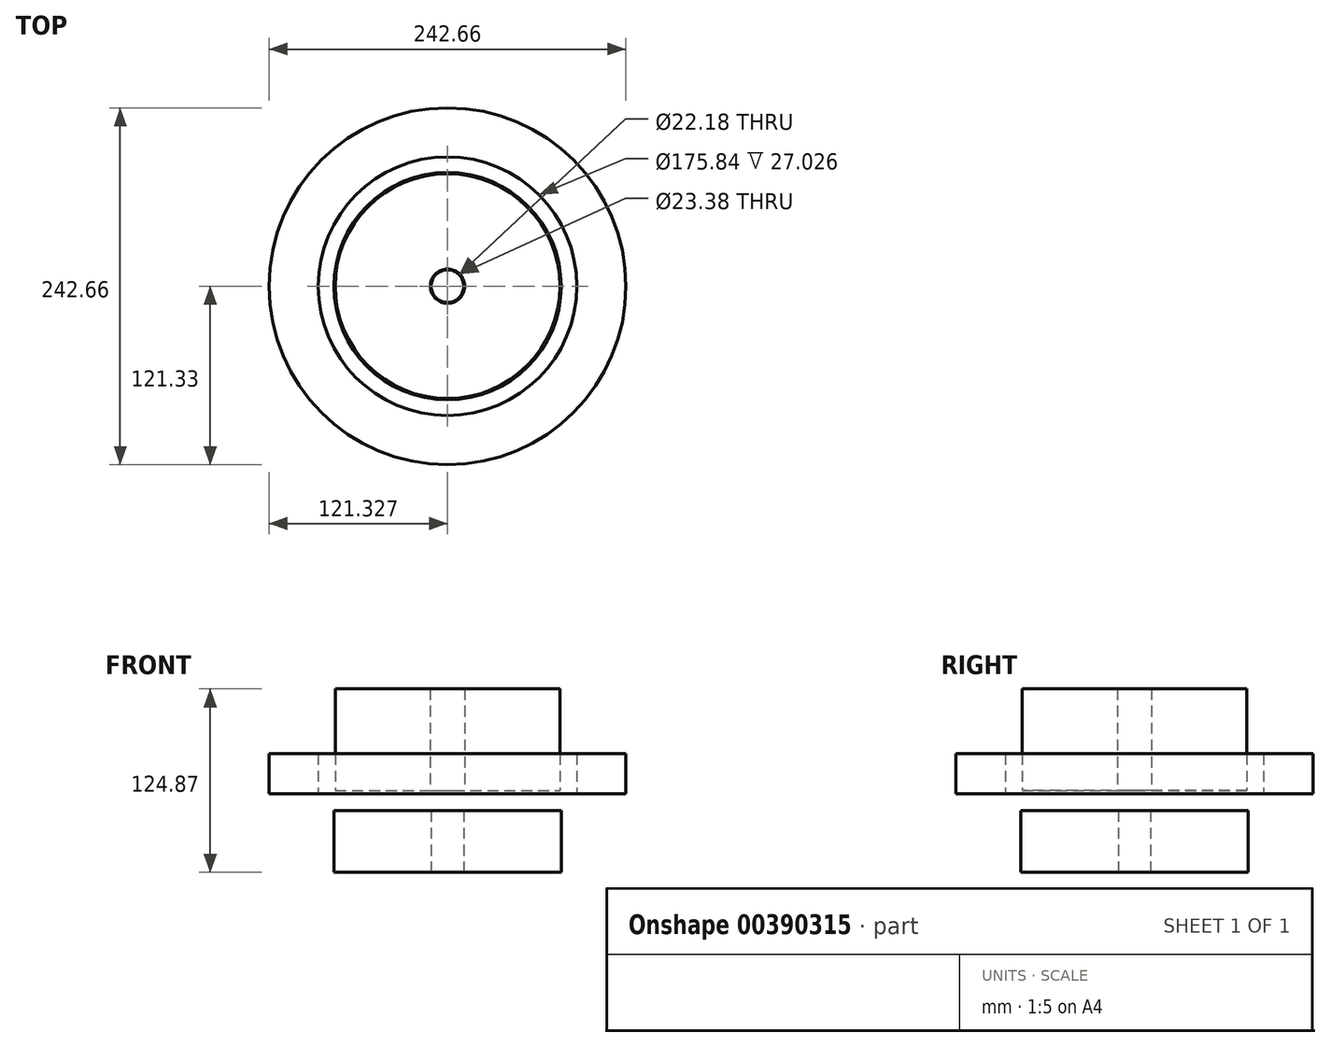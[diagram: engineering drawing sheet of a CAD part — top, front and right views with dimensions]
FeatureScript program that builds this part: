
annotation { "Feature Type Name" : "Feature", "Feature Type Description" : "" }
export const myFeature = defineFeature(function(context is Context, id is Id, definition is map)
    precondition{}
    {
        {
            var Q0;
            Q0=qCreatedBy(makeId("Front.planeOp"),FACE);
            var sketch = newSketch(context, id + "F0", { "sketchPlane" : qUnion([Q0])});
            skLineSegment(sketch, "E0.bottom", {"start": v(-58.43, 16.25) * mm, "end": v(7.8, 16.25) * mm});
            skLineSegment(sketch, "E0.top", {"start": v(-58.43, -25.66) * mm, "end": v(7.8, -25.66) * mm});
            skLineSegment(sketch, "E0.left", {"start": v(-58.43, 16.25) * mm, "end": v(-58.43, -25.66) * mm});
            skLineSegment(sketch, "E0.right", {"start": v(7.8, 16.25) * mm, "end": v(7.8, -25.66) * mm});
            skLineSegment(sketch, "E1.bottom", {"start": v(-69.02, 27.96) * mm, "end": v(-102.43, 27.96) * mm});
            skLineSegment(sketch, "E1.top", {"start": v(-69.02, 54.99) * mm, "end": v(-102.43, 54.99) * mm});
            skLineSegment(sketch, "E1.left", {"start": v(-69.02, 27.96) * mm, "end": v(-69.02, 54.99) * mm});
            skLineSegment(sketch, "E1.right", {"start": v(-102.43, 27.96) * mm, "end": v(-102.43, 54.99) * mm});
            skLineSegment(sketch, "E2.bottom", {"start": v(30.59, 29.94) * mm, "end": v(95.3, 29.94) * mm});
            skLineSegment(sketch, "E2.top", {"start": v(30.59, 99.2) * mm, "end": v(95.3, 99.2) * mm});
            skLineSegment(sketch, "E2.left", {"start": v(30.59, 29.94) * mm, "end": v(30.59, 99.2) * mm});
            skLineSegment(sketch, "E2.right", {"start": v(95.3, 29.94) * mm, "end": v(95.3, 99.2) * mm});
            skLineSegment(sketch, "E3", {"start": v(18.9, 0) * mm, "end": v(18.9, 58) * mm, "construction": true});
            skSolve(sketch);
        }
        {
            var Q0;
            Q0 = qSketchRegion(id + "F0", true);
            var Q1;
            Q1=sQuery(id+"F0.wireOp",EDGE,"E3");
            revolve(context, id + "F1", {"entities" : qUnion([Q0]), "axis" : qUnion([Q1]), "revolveType" : RevolveType.FULL});
        }
    });
